# Revit family: SingleHungWindow
name_source: partatom
category: Windows
revit_build: Autodesk Revit LT 2016 (Build: 20150220_1215(x64)
units: mm (PartAtom-declared; Revit-internal decimal feet)

## family parameters
Always vertical = Yes
Cut with Voids When Loaded = Yes
Host = Wall
OmniClass Number = 23.30.20.00
OmniClass Title = Windows
Room Calculation Point = No
Shared = No

## types (21) — shared parameters
Analytic Construction = <None>
Frame Width = 0' - 1 1/2"
Upper Sash Recess depth (default) = 0' - 1"
Wall Closure = By host

## per-type parameters (varying)
| type | Default Sill Height | Height | Trim Projection | Trim Width | Width |
| 3050 | 2' - 0" | 5' - 0" | 0' - 0" | 0' - 0" | 3' - 0" |
| 2050 | 2' - 0" | 5' - 0" | 0' - 1" | 0' - 3" | 2' - 0" |
| 2850 | 2' - 0" | 5' - 0" | 0' - 0" | 0' - 0" | 2' - 8" |
| 2650 | 2' - 0" | 5' - 0" | 0' - 0" | 0' - 0" | 2' - 6" |
| 2060 | 1' - 0" | 6' - 0" | 0' - 0" | 0' - 0" | 2' - 0" |
| 3060 | 1' - 0" | 6' - 0" | 0' - 0" | 0' - 0" | 3' - 0" |
| 2660 | 1' - 0" | 6' - 0" | 0' - 0" | 0' - 0" | 2' - 6" |
| 2860 | 1' - 0" | 6' - 0" | 0' - 0" | 0' - 0" | 2' - 8" |
| 3030 | 4' - 0" | 3' - 0" | 0' - 0" | 0' - 0" | 3' - 0" |
| 3040 | 3' - 0" | 4' - 0" | 0' - 0" | 0' - 0" | 3' - 0" |
| 2030 | 4' - 0" | 3' - 0" | 0' - 0" | 0' - 0" | 2' - 0" |
| 2040 | 3' - 0" | 4' - 0" | 0' - 0" | 0' - 0" | 2' - 0" |
| 3860 | 1' - 0" | 6' - 0" | 0' - 0" | 0' - 0" | 3' - 8" |
| 3850 | 2' - 0" | 5' - 0" | 0' - 0" | 0' - 0" | 3' - 8" |
| 2440 | 3' - 0" | 4' - 0" | 0' - 0" | 0' - 0" | 2' - 4" |
| 2450 | 2' - 0" | 5' - 0" | 0' - 0" | 0' - 0" | 2' - 4" |
| 2460 | 1' - 0" | 6' - 0" | 0' - 0" | 0' - 0" | 2' - 4" |
| 1050 | 2' - 0" | 5' - 0" | 0' - 1" | 0' - 3" | 1' - 0" |
| 1650 | 2' - 0" | 5' - 0" | 0' - 1" | 0' - 3" | 1' - 6" |
| 1060 | 1' - 0" | 6' - 0" | 0' - 1" | 0' - 3" | 1' - 0" |
| 1660 | 1' - 0" | 6' - 0" | 0' - 1" | 0' - 3" | 1' - 6" |

## geometry (parser evidence)
native form markers: Blend x2, Sweep x3
no freeform markers — native parametric forms only
